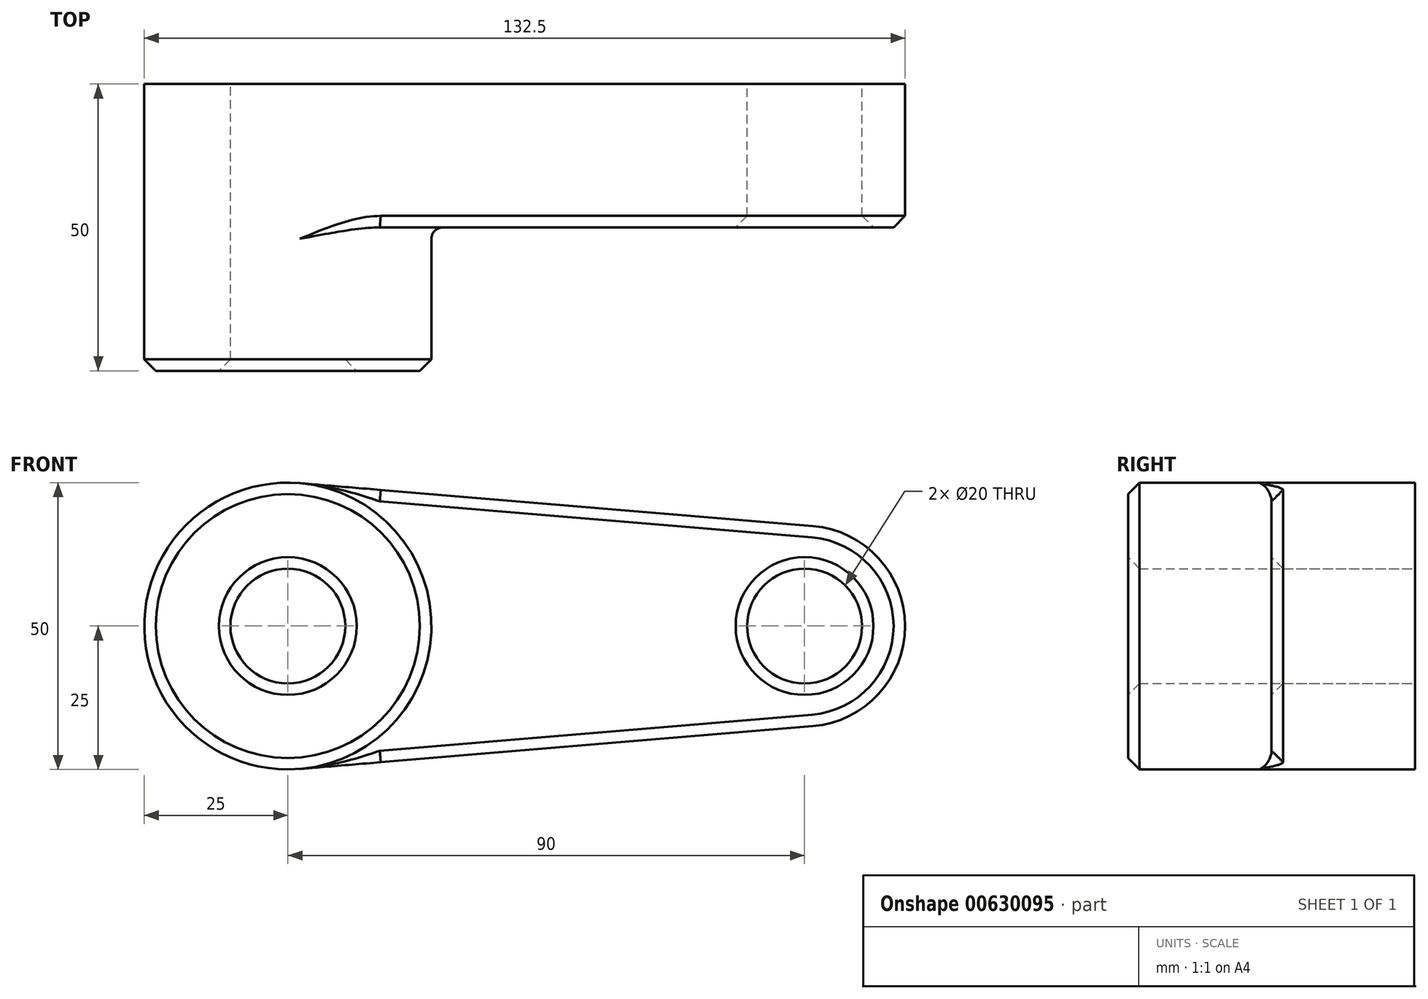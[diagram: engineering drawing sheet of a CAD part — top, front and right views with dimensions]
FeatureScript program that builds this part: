
annotation { "Feature Type Name" : "Feature", "Feature Type Description" : "" }
export const myFeature = defineFeature(function(context is Context, id is Id, definition is map)
    precondition{}
    {
        {
            var Q0;
            Q0=qCreatedBy(makeId("Front.planeOp"),FACE);
            var sketch = newSketch(context, id + "F0", { "sketchPlane" : qUnion([Q0])});
            skCircle(sketch, "E0", {"center": v(0, 0) * mm, "radius": 25 * mm});
            skCircle(sketch, "E1", {"center": v(90, 0) * mm, "radius": 17.5 * mm});
            skLineSegment(sketch, "E2", {"start": v(2.08, 24.91) * mm, "end": v(91.46, 17.44) * mm});
            skLineSegment(sketch, "E3", {"start": v(2.08, -24.91) * mm, "end": v(91.46, -17.44) * mm});
            skCircle(sketch, "E4", {"center": v(0, 0) * mm, "radius": 10 * mm});
            skCircle(sketch, "E5", {"center": v(90, 0) * mm, "radius": 10 * mm});
            skSolve(sketch);
        }
        {
            var Q0;
            Q0 = qSketchRegion(id + "F0", true);
            extrude(context, id + "F1", {"entities" : qUnion([Q0]), "depth" : 25 * mm, "offsetDistance" : 25 * mm});
        }
        {
            var Q0;
            Q0=makeQuery(id+"F0.imprint","IMPRINT",FACE,{"disambiguationData":[TD([[makeQuery(id+"F0.imprint","IMPRINT",EDGE,{"derivedFrom":sQuery(id+"F0.wireOp",EDGE,"E4")}),-1.0]])]});
            extrude(context, id + "F2", {"entities" : qUnion([Q0]), "operationType" : NewBodyOperationType.ADD, "depth" : 50 * mm, "offsetDistance" : 25 * mm});
        }
        {
            var Q0;
            Q0=makeQuery(id+"F2.opExtrude","CAP_EDGE",EDGE,{"disambiguationData":[OSD([sQuery(id+"F0.wireOp",EDGE,"E0")])],"isStart":false});
            var Q1;
            Q1=makeQuery(id+"F2.opExtrude","CAP_EDGE",EDGE,{"disambiguationData":[OSD([sQuery(id+"F0.wireOp",EDGE,"E4")])],"isStart":false});
            var Q2;
            Q2=makeQuery(id+"F1.opExtrude","CAP_EDGE",EDGE,{"disambiguationData":[OSD([sQuery(id+"F0.wireOp",EDGE,"E5")])],"isStart":false});
            chamfer(context, id + "F3", {"entities" : qUnion([Q0, Q1, Q2]), "width" : 2 * mm, "tangentPropagation" : true});
        }
        {
            var Q0;
            {var subQ0=sQuery(id+"F0.wireOp",EDGE,"E0");Q0=makeQuery(id+"F2.boolean.opBoolean","INTERSECT",EDGE,{"derivedFrom":[makeQuery(id+"F1.opExtrude","CAP_FACE",FACE,{"disambiguationData":[OSD([subQ0,sQuery(id+"F0.wireOp",EDGE,"E1"),sQuery(id+"F0.wireOp",EDGE,"E2"),sQuery(id+"F0.wireOp",EDGE,"E3"),sQuery(id+"F0.wireOp",EDGE,"E4"),sQuery(id+"F0.wireOp",EDGE,"E5")])],"isStart":false}),makeQuery(id+"F2.opExtrude","SWEPT_FACE",FACE,{"disambiguationData":[OSD([subQ0])]})]});}
            fillet(context, id + "F4", {"entities" : qUnion([Q0]), "radius" : 2 * mm, "tangentPropagation" : true, "allowEdgeOverflow" : false});
        }
        {
            var Q0;
            Q0=makeQuery(id+"F1.opExtrude","CAP_EDGE",EDGE,{"disambiguationData":[OSD([sQuery(id+"F0.wireOp",EDGE,"E3")])],"isStart":false});
            var Q1;
            Q1=makeQuery(id+"F1.opExtrude","CAP_EDGE",EDGE,{"disambiguationData":[OSD([sQuery(id+"F0.wireOp",EDGE,"E1")])],"isStart":false});
            var Q2;
            Q2=makeQuery(id+"F1.opExtrude","CAP_EDGE",EDGE,{"disambiguationData":[OSD([sQuery(id+"F0.wireOp",EDGE,"E2")])],"isStart":false});
            chamfer(context, id + "F5", {"entities" : qUnion([Q0, Q1, Q2]), "width" : 2 * mm, "tangentPropagation" : true});
        }
    });
